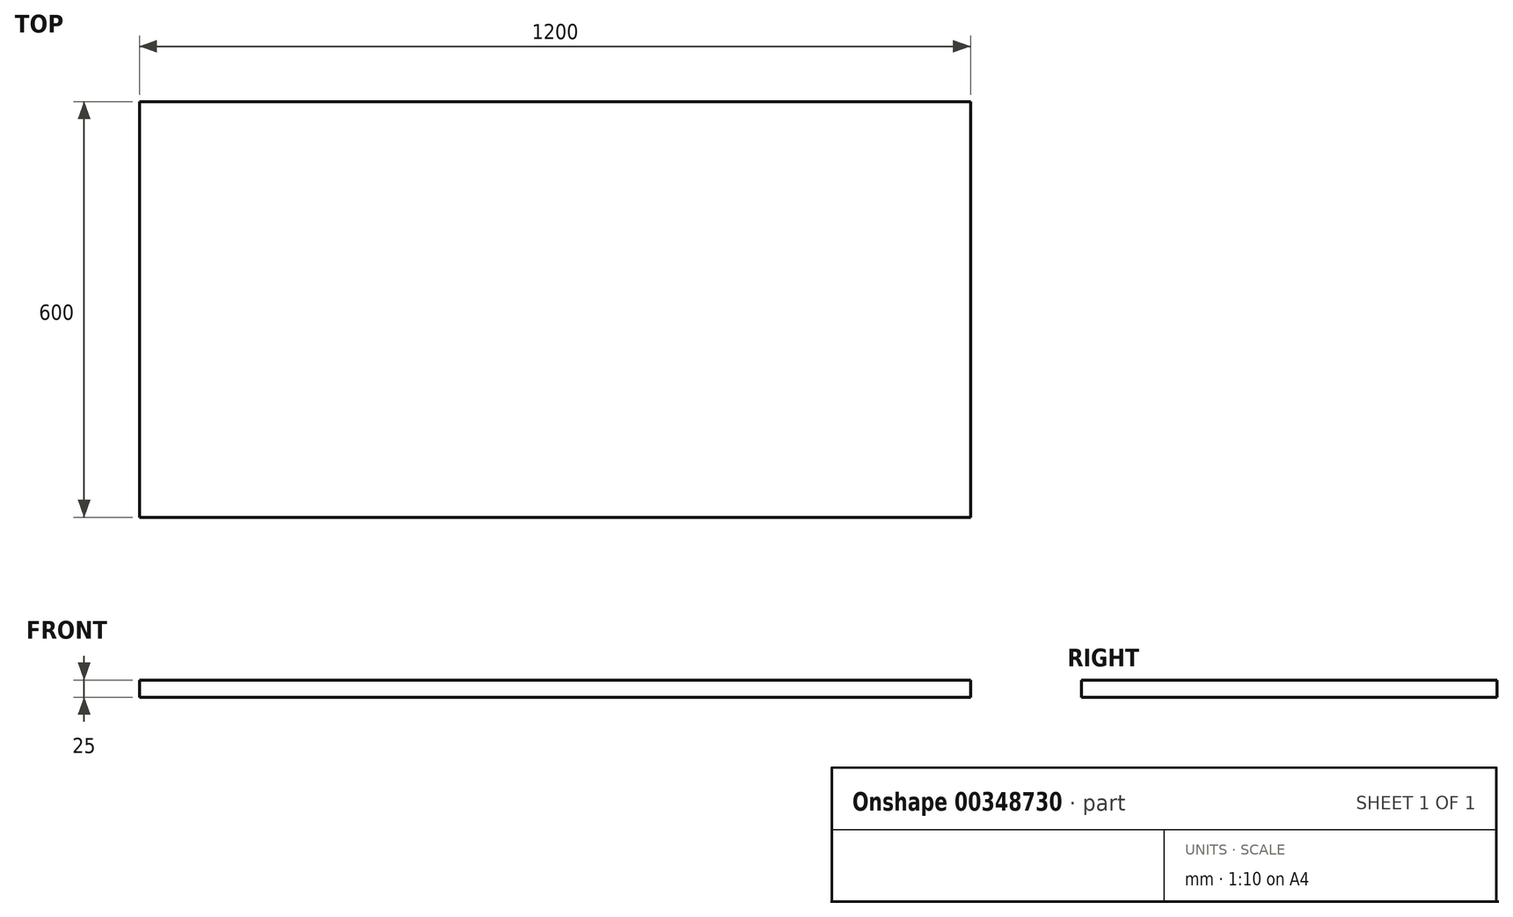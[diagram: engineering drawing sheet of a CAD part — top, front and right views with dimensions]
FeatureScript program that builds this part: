
annotation { "Feature Type Name" : "Feature", "Feature Type Description" : "" }
export const myFeature = defineFeature(function(context is Context, id is Id, definition is map)
    precondition{}
    {
        {
            var Q0;
            Q0=qCreatedBy(makeId("Top.planeOp"),FACE);
            var sketch = newSketch(context, id + "F0", { "sketchPlane" : qUnion([Q0])});
            skLineSegment(sketch, "E0.bottom", {"start": v(600, -300) * mm, "end": v(-600, -300) * mm});
            skLineSegment(sketch, "E0.top", {"start": v(600, 300) * mm, "end": v(-600, 300) * mm});
            skLineSegment(sketch, "E0.left", {"start": v(600, -300) * mm, "end": v(600, 300) * mm});
            skLineSegment(sketch, "E0.right", {"start": v(-600, -300) * mm, "end": v(-600, 300) * mm});
            skPoint(sketch, "E0.middle", {"position": v(0, 0) * mm});
            skSolve(sketch);
        }
        {
            var Q0;
            Q0=makeQuery(id+"F0.imprint","IMPRINT",FACE,{"disambiguationData":[TD([[makeQuery(id+"F0.imprint","IMPRINT",EDGE,{"derivedFrom":sQuery(id+"F0.wireOp",EDGE,"E0.bottom")}),-1.0]])]});
            extrude(context, id + "F1", {"entities" : qUnion([Q0]), "depth" : 25 * mm});
        }
    });
